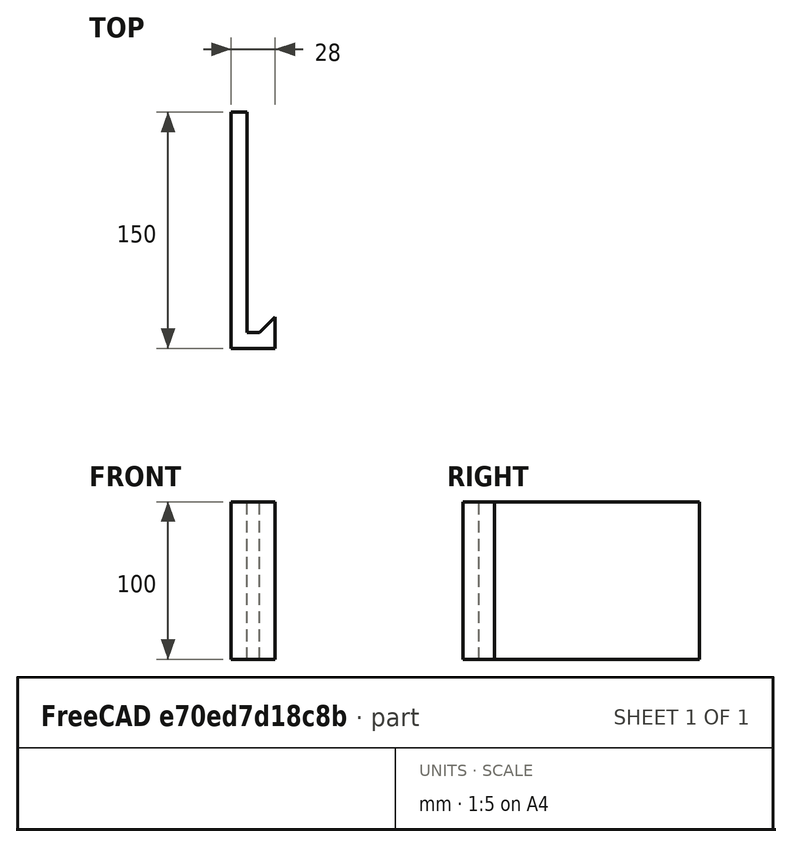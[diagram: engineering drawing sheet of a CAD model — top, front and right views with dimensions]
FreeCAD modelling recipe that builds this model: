
FCSTD DOCUMENT  (FreeCAD 0.17RUnknown)
Label: front
License: All rights reserved
LicenseURL: http://en.wikipedia.org/wiki/All_rights_reserved
objects: Sketcher::SketchObject×1, PartDesign::Pad×1, PartDesign::Body×1
note: 4 computed .brp shape members not serialized (recipe doc carries the construction recipe); baked Part::Feature solids carry a one-line shape summary decoded from their .brp

FEATURE [Sketcher::SketchObject] Sketch
  MapMode = 5
  Support = -> [XY_Plane]
  sketch-geometry (8):
    g0: LineSegment StartX=0 StartY=150 StartZ=0 EndX=0 EndY=0 EndZ=0
    g1: LineSegment StartX=0 StartY=0 StartZ=0 EndX=28 EndY=0 EndZ=0
    g2: LineSegment StartX=28 StartY=0 StartZ=0 EndX=28 EndY=20 EndZ=0
    g3: LineSegment StartX=28 StartY=20 StartZ=0 EndX=18 EndY=10 EndZ=0
    g4: LineSegment StartX=18 StartY=10 StartZ=0 EndX=10 EndY=10 EndZ=0
    g5: LineSegment StartX=10 StartY=10 StartZ=0 EndX=10 EndY=150 EndZ=0
    g6: LineSegment StartX=10 StartY=150 StartZ=0 EndX=0 EndY=150 EndZ=0
    g7: LineSegment [constr] StartX=18 StartY=10 StartZ=0 EndX=18 EndY=0 EndZ=0
  constraints (23):
    c: Coincident(g0,g1)
    c: Coincident(g1,g2)
    c: Coincident(g2,g3)
    c: Coincident(g4,g5)
    c: Coincident(g5,g6)
    c: Coincident(g6,g0)
    c: Coincident(g3,g4)
    c: Coincident(g0,g-1)
    c: PointOnObject(g1,g-1)
    c: PointOnObject(g0,g-2)
    c: Distance(g0) = 150
    c: Parallel(g0,g5)
    c: Parallel(g0,g2)
    c: Parallel(g4,g1)
    c: Parallel(g1,g6)
    c: Distance(g4) = 8
    c: Coincident(g7,g3)
    c: PointOnObject(g7,g1)
    c: Vertical(g7)
    c: Distance(g7,g1) = 10
    c: Distance(g7) = 10
    c: Distance(g2) = 20
    c: Distance(g6) = 10
FEATURE [PartDesign::Pad] Pad
  Length = 100
  Length2 = 100
  Profile = -> Sketch
  Type = 0
FEATURE [PartDesign::Body] Body
  Group = -> [Sketch,Pad]
  Origin = -> Origin
  Tip = -> Pad
